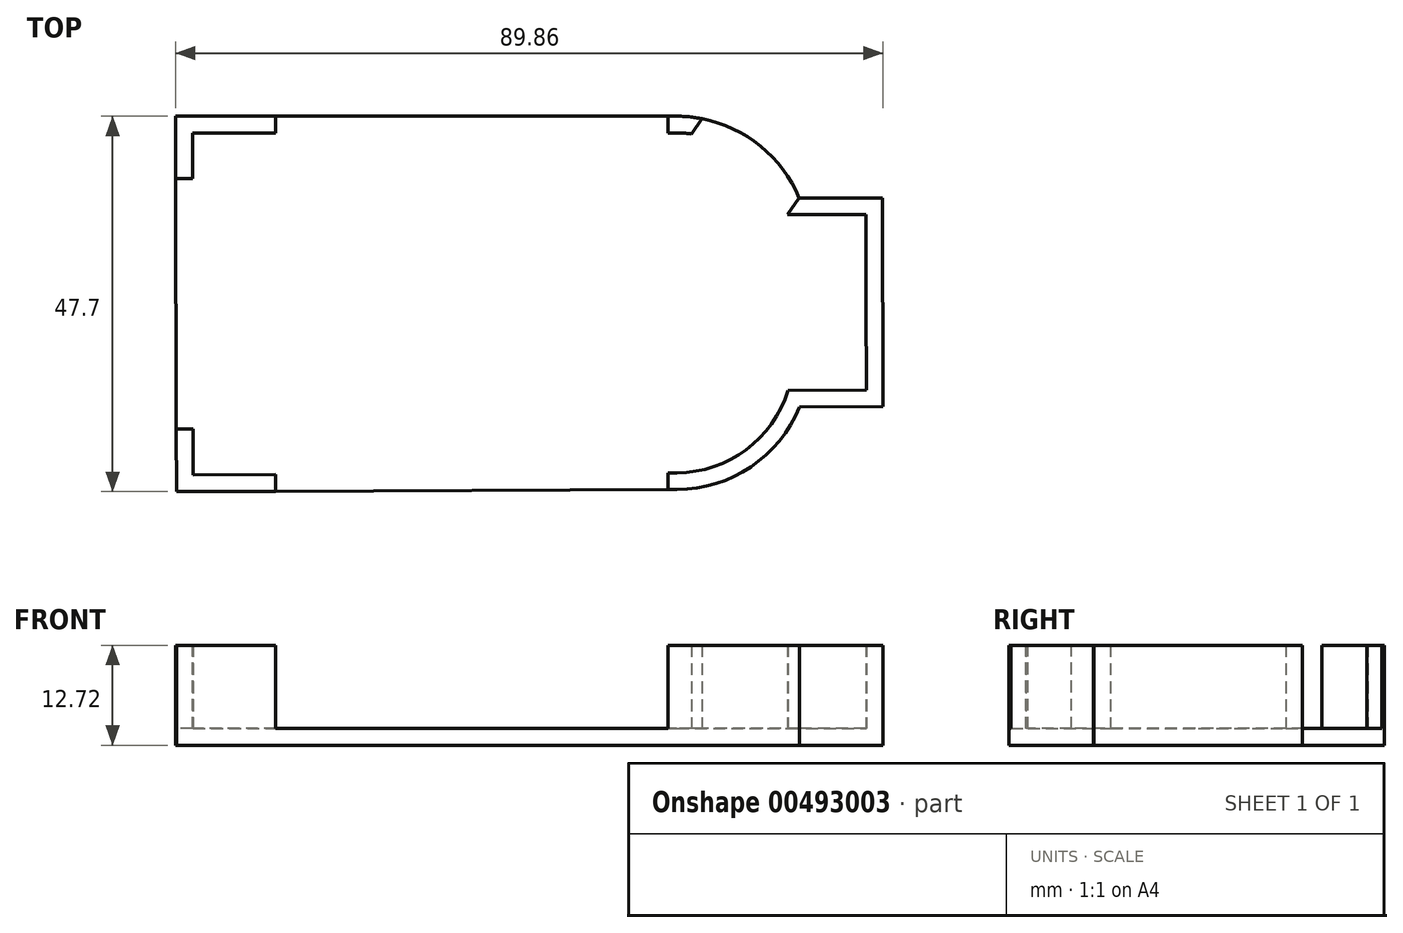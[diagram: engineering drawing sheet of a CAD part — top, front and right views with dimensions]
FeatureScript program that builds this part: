
annotation { "Feature Type Name" : "Feature", "Feature Type Description" : "" }
export const myFeature = defineFeature(function(context is Context, id is Id, definition is map)
    precondition{}
    {
        {
            var Q0;
            Q0=qCreatedBy(makeId("Top.planeOp"),FACE);
            var sketch = newSketch(context, id + "F0", { "sketchPlane" : qUnion([Q0])});
            skLineSegment(sketch, "E0", {"start": v(0, 22.5) * mm, "end": v(60, 22.5) * mm});
            skLineSegment(sketch, "E1", {"start": v(84.72, 12.68) * mm, "end": v(74.72, 12.68) * mm});
            skArc(sketch, "E2", {"start": v(74.72, 12.68) * mm, "mid": v(68.85, 19.82) * mm, "end": v(60, 22.5) * mm});
            skArc(sketch, "E3.MirrorCS", {"start": v(74.78, -12.36) * mm, "mid": v(68.93, -19.52) * mm, "end": v(60.1, -22.24) * mm});
            skLineSegment(sketch, "E4.MirrorCS", {"start": v(84.78, -12.32) * mm, "end": v(74.78, -12.36) * mm});
            skLineSegment(sketch, "E5.MirrorCS", {"start": v(0.1, -22.5) * mm, "end": v(60.1, -22.24) * mm});
            skLineSegment(sketch, "E6", {"start": v(0, 22.5) * mm, "end": v(0.1, -22.5) * mm});
            skLineSegment(sketch, "E7", {"start": v(84.78, -12.32) * mm, "end": v(84.72, 12.68) * mm});
            skSolve(sketch);
        }
        {
            var Q0;
            Q0=qSketchRegion(id+"F0",true);
            extrude(context, id + "F1", {"entities" : qUnion([Q0]), "depth" : 2 * mm});
        }
        {
            var Q0;
            Q0=makeQuery(id+"F1.opExtrude","CAP_FACE",FACE,{"disambiguationData":[OSD([sQuery(id+"F0.wireOp",EDGE,"uTuGEVu6-6x9x-pK5a-ensT-m59ZLZzseQzN"),sQuery(id+"F0.wireOp",EDGE,"pB7aODw4-huN5-U1fY-wkJ1-6sLhXuAIPxoM"),sQuery(id+"F0.wireOp",EDGE,"E0"),sQuery(id+"F0.wireOp",EDGE,"E1"),sQuery(id+"F0.wireOp",EDGE,"E2"),sQuery(id+"F0.wireOp",EDGE,"E3.MirrorCS"),sQuery(id+"F0.wireOp",EDGE,"d761203e-bd1e-49a6-a6b8-962b75256f741.MirrorCS"),sQuery(id+"F0.wireOp",EDGE,"d761203e-bd1e-49a6-a6b8-962b75256f742.MirrorCS"),sQuery(id+"F0.wireOp",EDGE,"E4.MirrorCS"),sQuery(id+"F0.wireOp",EDGE,"E5.MirrorCS")])],"isStart":false});
            var sketch = newSketch(context, id + "F2", { "sketchPlane" : qUnion([Q0])});
            skLineSegment(sketch, "E8.0", {"start": v(60, 20.5) * mm, "end": v(2, 20.5) * mm});
            skArc(sketch, "E8.1", {"start": v(73.32, 10.68) * mm, "mid": v(68.27, 17.78) * mm, "end": v(60, 20.5) * mm});
            skLineSegment(sketch, "E8.3", {"start": v(82.72, 10.68) * mm, "end": v(73.32, 10.68) * mm});
            skLineSegment(sketch, "E8.4", {"start": v(82.72, 0.18) * mm, "end": v(82.72, 10.68) * mm});
            skLineSegment(sketch, "E8.5", {"start": v(82.77, -10.32) * mm, "end": v(82.72, 0.18) * mm});
            skLineSegment(sketch, "E8.7", {"start": v(2.09, -20.5) * mm, "end": v(60.09, -20.24) * mm});
            skArc(sketch, "E8.8", {"start": v(60.09, -20.24) * mm, "mid": v(68.35, -17.48) * mm, "end": v(73.37, -10.36) * mm});
            skLineSegment(sketch, "E8.9", {"start": v(73.37, -10.36) * mm, "end": v(82.77, -10.32) * mm});
            skLineSegment(sketch, "E9", {"start": v(2, 20.5) * mm, "end": v(2.09, -20.5) * mm});
            skSolve(sketch);
        }
        {
            var Q0;
            Q0=makeQuery(id+"F2.imprint","IMPRINT",FACE,{"disambiguationData":[TD([[makeQuery(id+"F2.imprint","IMPRINT",EDGE,{"derivedFrom":sQuery(id+"F2.wireOp",EDGE,"E8.0")}),-1.0]])]});
            extrude(context, id + "F3", {"entities" : qUnion([Q0]), "operationType" : NewBodyOperationType.ADD, "depth" : 10 * mm});
        }
        {
            var Q0;
            {var subQ0=sQuery(id+"F0.wireOp",EDGE,"E6");Q0=makeQuery(id+"F3.boolean.opBoolean","MERGE",FACE,{"derivedFrom":[makeQuery(id+"F1.opExtrude","SWEPT_FACE",FACE,{"disambiguationData":[OSD([subQ0])]}),makeQuery(id+"F3.opExtrude","SWEPT_FACE",FACE,{"disambiguationData":[OSD([subQ0])]})]});}
            var sketch = newSketch(context, id + "F4", { "sketchPlane" : qUnion([Q0])});
            skLineSegment(sketch, "E10.bottom", {"start": v(-15, 2) * mm, "end": v(15, 2) * mm});
            skLineSegment(sketch, "E10.top", {"start": v(15, 52) * mm, "end": v(-15, 52) * mm});
            skLineSegment(sketch, "E10.left", {"start": v(-15, 2) * mm, "end": v(-15, 52) * mm});
            skLineSegment(sketch, "E10.right", {"start": v(15, 2) * mm, "end": v(15, 52) * mm});
            skPoint(sketch, "E11", {"position": v(0, 2) * mm});
            skSolve(sketch);
        }
        {
            var Q0;
            Q0=makeQuery(id+"F4.imprint","IMPRINT",FACE,{"disambiguationData":[TD([[makeQuery(id+"F4.imprint","IMPRINT",EDGE,{"derivedFrom":sQuery(id+"F4.wireOp",EDGE,"E10.bottom")}),1.0]])]});
            extrude(context, id + "F5", {"entities" : qUnion([Q0]), "operationType" : NewBodyOperationType.REMOVE, "endBound" : BoundingType.UP_TO_NEXT, "oppositeDirection" : true, "depth" : 25 * mm});
        }
        {
            var Q0;
            Q0=qSketchRegion(id+"F4",true);
            extrude(context, id + "F6", {"entities" : qUnion([Q0]), "operationType" : NewBodyOperationType.REMOVE, "oppositeDirection" : true, "depth" : 25 * mm});
        }
        {
            var Q0;
            Q0=makeQuery(id+"F6.boolean.opBoolean","MERGE",FACE,{"derivedFrom":[makeQuery(id+"F1.opExtrude","CAP_FACE",FACE,{"disambiguationData":[OSD([sQuery(id+"F0.wireOp",EDGE,"E0"),sQuery(id+"F0.wireOp",EDGE,"E1"),sQuery(id+"F0.wireOp",EDGE,"E2"),sQuery(id+"F0.wireOp",EDGE,"E3.MirrorCS"),sQuery(id+"F0.wireOp",EDGE,"E4.MirrorCS"),sQuery(id+"F0.wireOp",EDGE,"E5.MirrorCS"),sQuery(id+"F0.wireOp",EDGE,"E6"),sQuery(id+"F0.wireOp",EDGE,"E7")])],"isStart":false}),makeQuery(id+"F6.opExtrude","SWEPT_FACE",FACE,{"disambiguationData":[OSD([sQuery(id+"F4.wireOp",EDGE,"E10.bottom")])]})]});
            var sketch = newSketch(context, id + "F7", { "sketchPlane" : qUnion([Q0])});
            skLineSegment(sketch, "E12", {"start": v(69.7, 5.5) * mm, "end": v(86.47, 29.46) * mm});
            skLineSegment(sketch, "E13", {"start": v(86.47, 29.46) * mm, "end": v(73.7, 37.38) * mm});
            skLineSegment(sketch, "E14", {"start": v(73.7, 37.38) * mm, "end": v(56.92, 13.41) * mm});
            skLineSegment(sketch, "E15", {"start": v(56.92, 13.41) * mm, "end": v(69.7, 5.5) * mm});
            skSolve(sketch);
        }
        {
            var Q0;
            Q0=qSketchRegion(id+"F7",true);
            extrude(context, id + "F8", {"entities" : qUnion([Q0]), "operationType" : NewBodyOperationType.REMOVE, "depth" : 50 * mm});
        }
        {
            var Q0;
            {var subQ0=sQuery(id+"F0.wireOp",EDGE,"E0");Q0=makeQuery(id+"F3.boolean.opBoolean","MERGE",FACE,{"derivedFrom":[makeQuery(id+"F1.opExtrude","SWEPT_FACE",FACE,{"disambiguationData":[OSD([subQ0])]}),makeQuery(id+"F3.opExtrude","SWEPT_FACE",FACE,{"disambiguationData":[OSD([subQ0])]})]});}
            var sketch = newSketch(context, id + "F9", { "sketchPlane" : qUnion([Q0])});
            skLineSegment(sketch, "E16.bottom", {"start": v(-59, 2) * mm, "end": v(-12, 2) * mm});
            skLineSegment(sketch, "E16.top", {"start": v(-59, 12) * mm, "end": v(-12, 12) * mm});
            skLineSegment(sketch, "E16.left", {"start": v(-59, 2) * mm, "end": v(-59, 12) * mm});
            skLineSegment(sketch, "E16.right", {"start": v(-12, 2) * mm, "end": v(-12, 12) * mm});
            skSolve(sketch);
        }
        {
            var Q0;
            Q0=qSketchRegion(id+"F9",true);
            extrude(context, id + "F10", {"entities" : qUnion([Q0]), "operationType" : NewBodyOperationType.REMOVE, "endBound" : BoundingType.THROUGH_ALL, "oppositeDirection" : true, "depth" : 25 * mm});
        }
        {
            var Q0;
            Q0=makeQuery(id+"F1.opExtrude","SWEPT_BODY",BODY,{"disambiguationData":[OSD([sQuery(id+"F0.wireOp",EDGE,"E0"),sQuery(id+"F0.wireOp",EDGE,"E1"),sQuery(id+"F0.wireOp",EDGE,"E2"),sQuery(id+"F0.wireOp",EDGE,"E3.MirrorCS"),sQuery(id+"F0.wireOp",EDGE,"E4.MirrorCS"),sQuery(id+"F0.wireOp",EDGE,"E5.MirrorCS"),sQuery(id+"F0.wireOp",EDGE,"E6"),sQuery(id+"F0.wireOp",EDGE,"E7")])]});
            var Q1;
            Q1=qCreatedBy(makeId("Origin.pointOp"),VERTEX);
            transform(context, id + "F11", {"entities" : qUnion([Q0]), "transformType" : TransformType.SCALE_UNIFORMLY, "scale" : 1.06, "scalePoint" : qUnion([Q1]), "makeCopy" : false});
        }
    });
